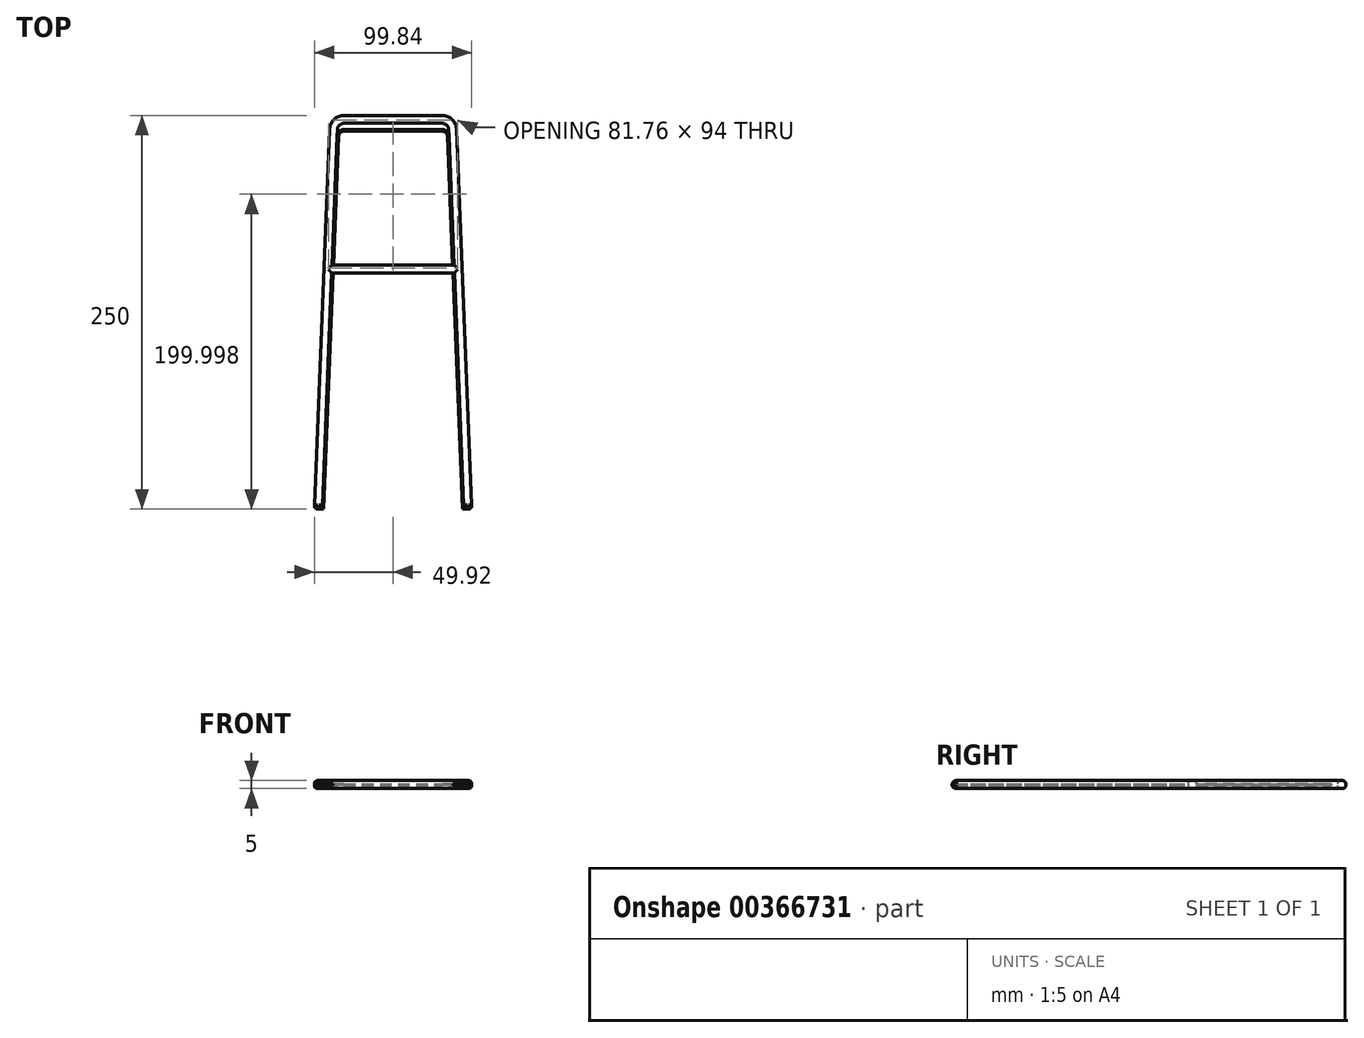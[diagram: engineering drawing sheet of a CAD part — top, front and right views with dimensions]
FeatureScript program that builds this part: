
annotation { "Feature Type Name" : "Feature", "Feature Type Description" : "" }
export const myFeature = defineFeature(function(context is Context, id is Id, definition is map)
    precondition{}
    {
        {
            var Q0;
            Q0=qCreatedBy(makeId("Top.planeOp"),FACE);
            var sketch = newSketch(context, id + "F0", { "sketchPlane" : qUnion([Q0])});
            skLineSegment(sketch, "E0", {"start": v(-50, 0) * mm, "end": v(-45, 0) * mm});
            skLineSegment(sketch, "E1", {"start": v(50, 0) * mm, "end": v(45, 0) * mm});
            skLineSegment(sketch, "E2", {"start": v(0, 150) * mm, "end": v(-39, 150) * mm});
            skLineSegment(sketch, "E3", {"start": v(-39, 150) * mm, "end": v(39, 150) * mm});
            skLineSegment(sketch, "E4", {"start": v(-38.8, 155) * mm, "end": v(38.8, 155) * mm});
            skLineSegment(sketch, "E5", {"start": v(39, 150) * mm, "end": v(45, 0) * mm});
            skLineSegment(sketch, "E6", {"start": v(-45, 0) * mm, "end": v(-39, 150) * mm});
            skPoint(sketch, "E7.endSnap0", {"position": v(0, 245) * mm});
            skArc(sketch, "E8", {"start": v(-31.36, 241) * mm, "mid": v(-34.24, 239.84) * mm, "end": v(-35.52, 237) * mm});
            skArc(sketch, "E9.MirrorCS", {"start": v(31.36, 241) * mm, "mid": v(34.24, 239.84) * mm, "end": v(35.52, 237) * mm});
            skLineSegment(sketch, "E10", {"start": v(-31.36, 241) * mm, "end": v(31.36, 241) * mm});
            skArc(sketch, "E11.0", {"start": v(31.36, 240) * mm, "mid": v(33.55, 239.12) * mm, "end": v(34.52, 236.96) * mm});
            skArc(sketch, "E12.MirrorCS", {"start": v(-31.36, 240) * mm, "mid": v(-33.55, 239.12) * mm, "end": v(-34.52, 236.96) * mm});
            skLineSegment(sketch, "E13", {"start": v(-31.36, 240) * mm, "end": v(31.36, 240) * mm});
            skLineSegment(sketch, "E14", {"start": v(37.8, 155) * mm, "end": v(34.52, 236.96) * mm});
            skLineSegment(sketch, "E15", {"start": v(-37.8, 155) * mm, "end": v(-34.52, 236.96) * mm});
            skLineSegment(sketch, "E16", {"start": v(44, 0) * mm, "end": v(38, 150) * mm});
            skLineSegment(sketch, "E17", {"start": v(35.52, 237) * mm, "end": v(38.8, 155) * mm});
            skLineSegment(sketch, "E18", {"start": v(-44, 0) * mm, "end": v(-38, 150) * mm});
            skLineSegment(sketch, "E19", {"start": v(-45, 0) * mm, "end": v(-44, 0) * mm});
            skLineSegment(sketch, "E20", {"start": v(45, 0) * mm, "end": v(44, 0) * mm});
            skArc(sketch, "E21", {"start": v(-31.2, 245) * mm, "mid": v(-34.08, 243.83) * mm, "end": v(-35.36, 241) * mm});
            skArc(sketch, "E22", {"start": v(-31, 250) * mm, "mid": v(-37.49, 247.39) * mm, "end": v(-40.36, 241) * mm});
            skLineSegment(sketch, "E23", {"start": v(0, 245) * mm, "end": v(0, 150) * mm, "construction": true});
            skArc(sketch, "E24.MirrorCS", {"start": v(31.2, 245) * mm, "mid": v(34.08, 243.83) * mm, "end": v(35.36, 241) * mm});
            skArc(sketch, "E25.MirrorCS", {"start": v(31, 250) * mm, "mid": v(37.49, 247.39) * mm, "end": v(40.36, 241) * mm});
            skLineSegment(sketch, "E26", {"start": v(40.36, 241) * mm, "end": v(50, 0) * mm});
            skLineSegment(sketch, "E27", {"start": v(-31, 250) * mm, "end": v(31, 250) * mm});
            skLineSegment(sketch, "E28", {"start": v(-31.2, 245) * mm, "end": v(31.2, 245) * mm});
            skLineSegment(sketch, "E29", {"start": v(-35.36, 241) * mm, "end": v(-38.8, 155) * mm});
            skLineSegment(sketch, "E30", {"start": v(-38.8, 155) * mm, "end": v(-35.52, 237) * mm});
            skLineSegment(sketch, "E31", {"start": v(-40.36, 241) * mm, "end": v(-50, 0) * mm});
            skLineSegment(sketch, "E32", {"start": v(35.36, 241) * mm, "end": v(38.8, 155) * mm});
            skSolve(sketch);
        }
        {
            var Q0;
            Q0=makeQuery(id+"F0.imprint","IMPRINT",FACE,{"disambiguationData":[TD([[makeQuery(id+"F0.imprint","IMPRINT",EDGE,{"derivedFrom":sQuery(id+"F0.wireOp",EDGE,"E0")}),1.0]])]});
            extrude(context, id + "F1", {"entities" : qUnion([Q0]), "endBound" : BoundingType.SYMMETRIC, "depth" : 5 * mm});
        }
        {
            var Q0;
            Q0=makeQuery(id+"F1.opExtrude","CAP_EDGE",EDGE,{"disambiguationData":[OSD([sQuery(id+"F0.wireOp",EDGE,"E1")])],"isStart":true});
            var Q1;
            Q1=makeQuery(id+"F1.opExtrude","CAP_EDGE",EDGE,{"disambiguationData":[OSD([sQuery(id+"F0.wireOp",EDGE,"E0")])],"isStart":true});
            var Q2;
            Q2=makeQuery(id+"F1.opExtrude","CAP_EDGE",EDGE,{"disambiguationData":[OSD([sQuery(id+"F0.wireOp",EDGE,"E1")])],"isStart":false});
            var Q3;
            Q3=makeQuery(id+"F1.opExtrude","CAP_EDGE",EDGE,{"disambiguationData":[OSD([sQuery(id+"F0.wireOp",EDGE,"E0")])],"isStart":false});
            fillet(context, id + "F2", {"entities" : qUnion([Q0, Q1, Q2, Q3]), "radius" : 2.5 * mm, "tangentPropagation" : true, "allowEdgeOverflow" : false});
        }
        {
            var Q0;
            Q0=makeQuery(id+"F0.imprint","IMPRINT",FACE,{"disambiguationData":[TD([[makeQuery(id+"F0.imprint","IMPRINT",EDGE,{"derivedFrom":sQuery(id+"F0.wireOp",EDGE,"E8")}),1.0]])]});
            extrude(context, id + "F3", {"entities" : qUnion([Q0]), "operationType" : NewBodyOperationType.ADD, "endBound" : BoundingType.SYMMETRIC, "depth" : 1 * mm});
        }
        {
            var Q0;
            {var subQ0=sQuery(id+"F0.wireOp",EDGE,"E6");Q0=makeQuery(id+"F0.imprint","IMPRINT",FACE,{"disambiguationData":[TD([[makeQuery(id+"F0.imprint","IMPRINT",EDGE,{"derivedFrom":subQ0}),-1.0]])]});}
            extrude(context, id + "F4", {"entities" : qUnion([Q0]), "operationType" : NewBodyOperationType.ADD, "endBound" : BoundingType.SYMMETRIC, "depth" : 1 * mm});
        }
        {
            var Q0;
            {var subQ0=sQuery(id+"F0.wireOp",EDGE,"E5");Q0=makeQuery(id+"F0.imprint","IMPRINT",FACE,{"disambiguationData":[TD([[makeQuery(id+"F0.imprint","IMPRINT",EDGE,{"derivedFrom":subQ0}),-1.0]])]});}
            extrude(context, id + "F5", {"entities" : qUnion([Q0]), "operationType" : NewBodyOperationType.ADD, "endBound" : BoundingType.SYMMETRIC, "depth" : 1 * mm});
        }
        {
            var Q0;
            Q0=makeQuery(id+"F1.opExtrude","CAP_EDGE",EDGE,{"disambiguationData":[OSD([sQuery(id+"F0.wireOp",EDGE,"E26")])],"isStart":false});
            var Q1;
            Q1=makeQuery(id+"F1.opExtrude","CAP_EDGE",EDGE,{"disambiguationData":[OSD([sQuery(id+"F0.wireOp",EDGE,"E28")])],"isStart":false});
            var Q2;
            Q2=makeQuery(id+"F1.opExtrude","CAP_EDGE",EDGE,{"disambiguationData":[OSD([sQuery(id+"F0.wireOp",EDGE,"E3")])],"isStart":false});
            var Q3;
            Q3=makeQuery(id+"F1.opExtrude","CAP_EDGE",EDGE,{"disambiguationData":[OSD([sQuery(id+"F0.wireOp",EDGE,"E6")])],"isStart":false});
            var Q4;
            Q4=makeQuery(id+"F1.opExtrude","CAP_EDGE",EDGE,{"disambiguationData":[OSD([sQuery(id+"F0.wireOp",EDGE,"E31")])],"isStart":false});
            var Q5;
            Q5=makeQuery(id+"F1.opExtrude","CAP_EDGE",EDGE,{"disambiguationData":[OSD([sQuery(id+"F0.wireOp",EDGE,"E26")])],"isStart":false});
            var Q6;
            Q6=makeQuery(id+"F1.opExtrude","CAP_EDGE",EDGE,{"disambiguationData":[OSD([sQuery(id+"F0.wireOp",EDGE,"E26")])],"isStart":true});
            var Q7;
            Q7=makeQuery(id+"F1.opExtrude","CAP_EDGE",EDGE,{"disambiguationData":[OSD([sQuery(id+"F0.wireOp",EDGE,"E5")])],"isStart":false});
            var Q8;
            Q8=makeQuery(id+"F1.opExtrude","CAP_EDGE",EDGE,{"disambiguationData":[OSD([sQuery(id+"F0.wireOp",EDGE,"E6")])],"isStart":true});
            var Q9;
            Q9=makeQuery(id+"F1.opExtrude","CAP_EDGE",EDGE,{"disambiguationData":[OSD([sQuery(id+"F0.wireOp",EDGE,"E3")])],"isStart":true});
            var Q10;
            Q10=makeQuery(id+"F1.opExtrude","CAP_EDGE",EDGE,{"disambiguationData":[OSD([sQuery(id+"F0.wireOp",EDGE,"E4")])],"isStart":true});
            var Q11;
            Q11=makeQuery(id+"F1.opExtrude","CAP_EDGE",EDGE,{"disambiguationData":[OSD([sQuery(id+"F0.wireOp",EDGE,"E28")])],"isStart":true});
            var Q12;
            Q12=makeQuery(id+"F1.opExtrude","CAP_EDGE",EDGE,{"disambiguationData":[OSD([sQuery(id+"F0.wireOp",EDGE,"E27")])],"isStart":true});
            var Q13;
            Q13=makeQuery(id+"F1.opExtrude","CAP_FACE",FACE,{"disambiguationData":[OSD([sQuery(id+"F0.wireOp",EDGE,"E0"),sQuery(id+"F0.wireOp",EDGE,"E1"),sQuery(id+"F0.wireOp",EDGE,"E3"),sQuery(id+"F0.wireOp",EDGE,"E4"),sQuery(id+"F0.wireOp",EDGE,"E5"),sQuery(id+"F0.wireOp",EDGE,"E6"),sQuery(id+"F0.wireOp",EDGE,"E21"),sQuery(id+"F0.wireOp",EDGE,"E22"),sQuery(id+"F0.wireOp",EDGE,"E24.MirrorCS"),sQuery(id+"F0.wireOp",EDGE,"E25.MirrorCS"),sQuery(id+"F0.wireOp",EDGE,"E26"),sQuery(id+"F0.wireOp",EDGE,"E27"),sQuery(id+"F0.wireOp",EDGE,"E28"),sQuery(id+"F0.wireOp",EDGE,"E29"),sQuery(id+"F0.wireOp",EDGE,"E30"),sQuery(id+"F0.wireOp",EDGE,"E31"),sQuery(id+"F0.wireOp",EDGE,"E32")])],"isStart":true});
            var Q14;
            Q14=makeQuery(id+"F1.opExtrude","CAP_FACE",FACE,{"disambiguationData":[OSD([sQuery(id+"F0.wireOp",EDGE,"E0"),sQuery(id+"F0.wireOp",EDGE,"E1"),sQuery(id+"F0.wireOp",EDGE,"E3"),sQuery(id+"F0.wireOp",EDGE,"E4"),sQuery(id+"F0.wireOp",EDGE,"E5"),sQuery(id+"F0.wireOp",EDGE,"E6"),sQuery(id+"F0.wireOp",EDGE,"E21"),sQuery(id+"F0.wireOp",EDGE,"E22"),sQuery(id+"F0.wireOp",EDGE,"E24.MirrorCS"),sQuery(id+"F0.wireOp",EDGE,"E25.MirrorCS"),sQuery(id+"F0.wireOp",EDGE,"E26"),sQuery(id+"F0.wireOp",EDGE,"E27"),sQuery(id+"F0.wireOp",EDGE,"E28"),sQuery(id+"F0.wireOp",EDGE,"E29"),sQuery(id+"F0.wireOp",EDGE,"E30"),sQuery(id+"F0.wireOp",EDGE,"E31"),sQuery(id+"F0.wireOp",EDGE,"E32")])],"isStart":true});
            var Q15;
            Q15=makeQuery(id+"F1.opExtrude","CAP_FACE",FACE,{"disambiguationData":[OSD([sQuery(id+"F0.wireOp",EDGE,"E0"),sQuery(id+"F0.wireOp",EDGE,"E1"),sQuery(id+"F0.wireOp",EDGE,"E3"),sQuery(id+"F0.wireOp",EDGE,"E4"),sQuery(id+"F0.wireOp",EDGE,"E5"),sQuery(id+"F0.wireOp",EDGE,"E6"),sQuery(id+"F0.wireOp",EDGE,"E21"),sQuery(id+"F0.wireOp",EDGE,"E22"),sQuery(id+"F0.wireOp",EDGE,"E24.MirrorCS"),sQuery(id+"F0.wireOp",EDGE,"E25.MirrorCS"),sQuery(id+"F0.wireOp",EDGE,"E26"),sQuery(id+"F0.wireOp",EDGE,"E27"),sQuery(id+"F0.wireOp",EDGE,"E28"),sQuery(id+"F0.wireOp",EDGE,"E29"),sQuery(id+"F0.wireOp",EDGE,"E30"),sQuery(id+"F0.wireOp",EDGE,"E31"),sQuery(id+"F0.wireOp",EDGE,"E32")])],"isStart":false});
            fillet(context, id + "F6", {"entities" : qUnion([Q0, Q1, Q2, Q3, Q4, Q5, Q6, Q7, Q8, Q9, Q10, Q11, Q12, Q13, Q14, Q15]), "radius" : 2 * mm, "tangentPropagation" : true, "allowEdgeOverflow" : false});
        }
        {
            var Q0;
            Q0=makeQuery(id+"F3.opExtrude","CAP_EDGE",EDGE,{"disambiguationData":[OSD([sQuery(id+"F0.wireOp",EDGE,"E13")])],"isStart":true});
            var Q1;
            Q1=makeQuery(id+"F3.opExtrude","CAP_EDGE",EDGE,{"disambiguationData":[OSD([sQuery(id+"F0.wireOp",EDGE,"E13")])],"isStart":false});
            fillet(context, id + "F7", {"entities" : qUnion([Q0, Q1]), "radius" : 0.5 * mm, "tangentPropagation" : true, "allowEdgeOverflow" : false});
        }
    });
